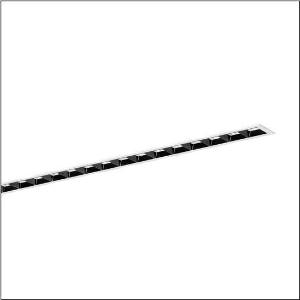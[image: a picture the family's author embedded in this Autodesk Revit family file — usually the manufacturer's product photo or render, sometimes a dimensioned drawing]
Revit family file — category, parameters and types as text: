
# Revit family: silica_r__21_51mx14tctaw_e0ea
name_source: partatom
category: Lighting Fixtures
units: mm (PartAtom-declared; Revit-internal decimal feet)

## family parameters
Cut with Voids When Loaded = No
Host = Face
Light Source = No
Part Type = Normal
Room Calculation Point = No
Round Connector Dimension = Use Diameter
Shared = No

## types (1)
- --- (1 x LED, 8200 lm, 81.1 W, 6500K)
    Apparent Load = 81 VA
    CIE Flux Codes = 74 94 99 100 100
    Color Rendering = 80
    Color Temperature = 6500K
    Default Elevation = 1800 mm
    Description = Silica® 21, office luminaire, primary light control with darklight reflector, of PMMA, black, light emission: direct distribution, primary light characteristic: asymmetric, installation type: recessed, LED, rated luminous flux: 8.200lm, luminous efficacy: 96lm/W, light colour: 8tw, colour temperature: 2700..6500K, with terminal, 3+2-pole, max. 2.5mm², mains connection: 220..240V, AC, 50/60Hz, rated input power: 85.2W, luminaire housing, of aluminium, traffic white (RAL 9016), length: 3.028mm, width: 79mm, height: 53mm, protection rating (complete): IP20, insulation class (complete): insulation class I (protective earthing), certification: CE, permissible operating ambient temperature: 0..+35°C, standard: EN 50419, packaging unit: 1 piece
    Height = 0 mm  [stored 0 ft]
    Lamp = 1 x LED
    Lamp Light Flux = 8200 lm
    Lamp Power = 81.1 W
    Lamp count = 1
    Length = 3027 mm
    Luminous efficacy = 101 lm/W
    Manufacturer = Siteco
    ModVariant = No
    Model = 51MX14TCTAW
    Mounting Place = Ceiling
    Mounting Type = Recessed
    Number of Poles = 1
    OnlyDefault = Yes
    Power Factor = 1
    Product Name = Silica® 21
    Product group = office luminaire | ceiling recessed
    ProductGroupID = 401
    Protection Class = Protection class I
    Protection Degree = IP 20
    RLX_Detail_Level = 1
    RLX_Emergency_Light_Flux = 0 lm
    RLX_Emergency_Type = 0
    RLX_Emergency_Type_DB = No
    RlxData = <blob elided: 60193 chars, md5=d67ddbdd>
    Socket = socket
    Standby Power = 0 W
    System Light Flux = 8200 lm
    System Power = 81 W
    Type Comments = individual setting
    Type Image = l_1297791.jpg
    URL = http://relux.com
    VarID = @adj_071347
    Voltage = 0 V
    Weight = 0.00 kg
    Width = 79 mm

note: [stored X ft] marks values corroborated as IEEE doubles in the binary element streams (Revit-internal decimal feet)

## geometry (parser evidence)
native form markers: Blend x4, Sweep x13
no freeform markers — native parametric forms only
